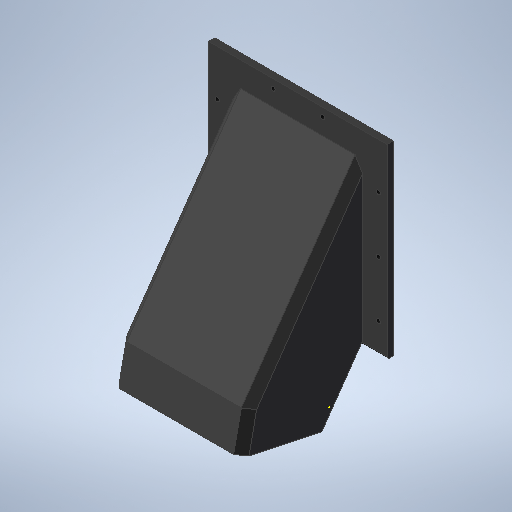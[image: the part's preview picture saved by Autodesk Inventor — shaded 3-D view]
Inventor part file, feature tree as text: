
AUTODESK INVENTOR PART (.ipt)
format: ipt  version: 2025.2 (Build 292293000, 293)  size: 630,784 bytes
history: native  units: in
note: dims shown in document units (in); Inventor stores cm internally (conversion verified against a paired STEP export)
features: sketch x29, extrude x25, plane x5, projected_geometry x5, move_body x1, chamfer x1, fillet x1, hole x1
ambient origin geometry x8: Origin, YZ Plane, XZ Plane, XY Plane, X Axis, Y Axis, Z Axis, Center Point
bodies: Solid1 (feature_tree)
feature tree (68):
  extrude  "Extrusion1"  Depth=0.1969in TaperAngle=0.0deg
  move_body  "Move Body1"
  plane  "Work Plane1"
  sketch  "Sketch5"  dims[d5=1.7717in d6=1.7717in d7=1.7717in d8=1.7717in d9=0.8108in d10=90.0deg d11=0.0787in d12=0.3701in d13=0.4252in d14=0.1362in d15=-0.0984in d16=-0.0591in d17=0.0in]
  plane  "Work Plane2"
  extrude  "Extrusion4"  TaperAngle=0.0deg  [1 undecoded]
  extrude  "Extrusion6"  Depth=0.2405in
  extrude  "Extrusion8"  Depth=2.5591in TaperAngle=0.0deg
  chamfer  "Chamfer1"  [1 undecoded]
  extrude  "Extrusion11"  Depth=0.1969in
  plane  "Work Plane3"
  extrude  "Extrusion13"  Depth=0.1969in TaperAngle=0.0deg
  plane  "Work Plane4"
  plane  "Work Plane6"
  extrude  "Extrusion21"  Depth=0.5027in
  extrude  "Extrusion22"  Depth=0.5027in
  extrude  "Extrusion25"  Depth=1.1811in TaperAngle=0.0deg
  extrude  "Extrusion26"  Depth=0.1969in
  sketch  "Sketch33"  dims[d100=3.7191in d101=2.7717in]
  extrude  "Extrusion27"  Depth=0.1969in TaperAngle=0.0deg
  extrude  "Extrusion28"  Depth=3.7191in
  sketch  "Sketch36"  dims[d124=0.9712in d125=0.0in d126=0.5906in d127=0.0in]
  extrude  "Extrusion29"  Depth=0.6299in TaperAngle=0.0deg
  extrude  "Extrusion30"  Depth=0.9331in
  extrude  "Extrusion31"  Depth=0.5906in TaperAngle=0.0deg
  sketch  "Sketch39"  dims[d139=0.3937in d140=0.0in d141=0.6299in]
  extrude  "Extrusion32"  Depth=11.3469in TaperAngle=0.0deg
  fillet  "Fillet1"  Radius=0.4331in
  extrude  "Extrusion33"  Depth=0.4331in
  extrude  "Extrusion34"  Depth=0.6299in
  extrude  "Extrusion35"  Depth=0.0787in
  sketch  "Sketch45"  dims[d160=0.1181in d161=0.0in d162=0.1969in d163=0.0in]
  extrude  "Extrusion36"  TaperAngle=0.0deg  [1 undecoded]
  extrude  "Extrusion37"  Depth=0.1181in TaperAngle=0.0deg
  extrude  "Extrusion38"  Depth=0.5906in
  extrude  "Extrusion40"  Depth=0.1969in TaperAngle=0.0deg
  extrude  "Extrusion41"  Depth=0.1181in TaperAngle=0.0deg
  extrude  "Extrusion43"  Depth=4.7244in TaperAngle=0.0deg
  sketch  "Sketch1"  dims[d1=0.5512in d2=0.1969in d3=0.0in]
  sketch  "Sketch6"  dims[d18=0.2749in d24=0.2405in]
  sketch  "Sketch8"  dims[d25=2.7559in d26=0.0in d29=2.5591in d30=0.0in d36=0.0in d37=0.0in]
  sketch  "Sketch12"  dims[d42=0.1969in d43=0.1969in]
  sketch  "Sketch15"  dims[d52=0.2362in d53=0.0787in d54=45.0deg d55=0.1969in d56=0.0in]
  sketch  "Sketch17"  dims[d59=0.5906in d60=0.0in d76=0.5027in]
  sketch  "Sketch27"  dims[d77=0.5027in d78=0.5027in]
  sketch  "Sketch28"  dims[d79=0.5027in d81=1.1811in d82=0.0in]
  sketch  "Sketch31"  dims[d83=0.0in d84=0.0in d91=0.1969in]
  sketch  "Sketch32"  dims[d94=0.1969in d95=0.0in d96=0.1969in d97=0.0in]
  sketch  "Sketch34"  dims[d112=1.9685in d113=0.6299in d114=0.0in]
  sketch  "Sketch35"  dims[d115=0.1575in d117=0.1575in d121=1.9685in d122=0.7874in d123=0.9331in]
  sketch  "Sketch37"  dims[d128=11.3469in d129=0.0in d130=11.3469in d131=0.0in d136=0.4331in]
  sketch  "Sketch38"  dims[d137=0.4331in d138=0.4331in]
  sketch  "Sketch40"  dims[d142=0.0787in d147=0.2756in]
  sketch  "Sketch41"  dims[d149=0.2756in d150=0.0in d151=0.0in]
  sketch  "Sketch42"  dims[d154=0.1969in d155=0.0in d156=0.1181in d157=0.0in]
  sketch  "Sketch44"  dims[d158=0.5906in d159=0.5906in]
  projected_geometry  "Projected Loop2"
  projected_geometry  "Projected Loop3"
  projected_geometry  "Projected Loop5"
  sketch  "Sketch46"  dims[d164=0.1181in d165=0.0in d166=0.5906in d167=0.0in]
  projected_geometry  "Projected Loop6"
  projected_geometry  "Projected Loop7"
  sketch  "Sketch47"  dims[d168=0.5906in d169=0.0in d170=4.7244in d171=0.0in]
  sketch  "Sketch49"  dims[d174=0.0in d175=0.0in d176=0.7313in d177=0.0in]
  sketch  "Sketch50"  dims[d186=0.0in d187=0.0in]
  sketch  "Sketch52"  dims[d38=0.0197in d39=0.0344in d57=0.0197in d58=0.0344in d178=0.0in d179=0.0in d180=0.0in d181=0.0in d188=0.0197in d189=0.0344in]
  sketch  "Sketch2"  dims[d4=0.315in]
  hole  "Hole1"  [1 undecoded]
note: 4 required parameter values undecoded (feature->parameter linkage not recoverable at this tier; creation-order binding heuristic only, values carry confidence <= 0.55)
